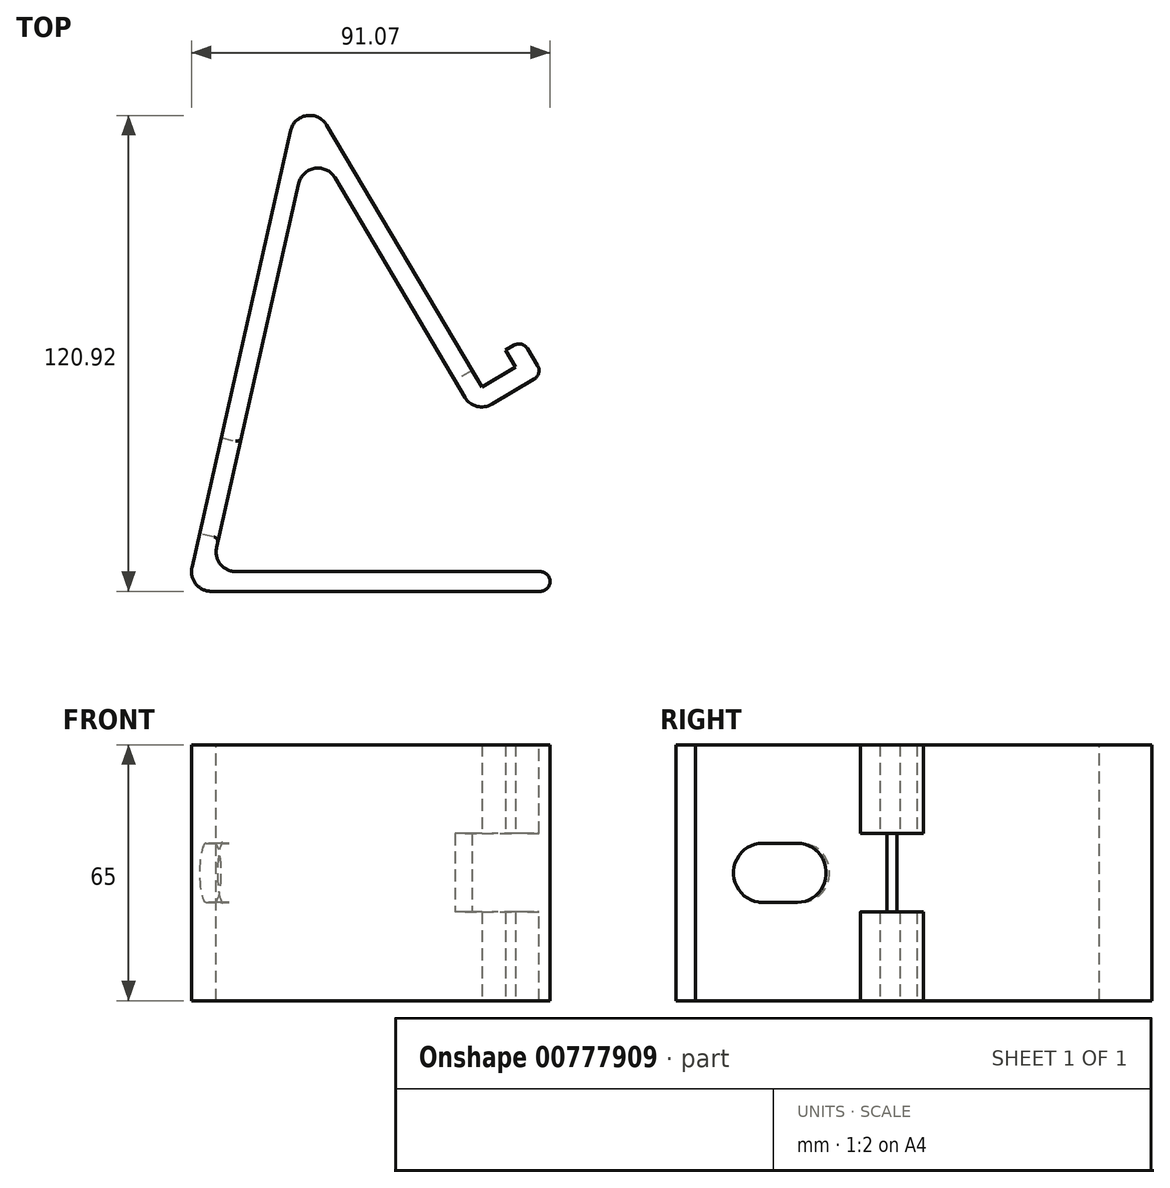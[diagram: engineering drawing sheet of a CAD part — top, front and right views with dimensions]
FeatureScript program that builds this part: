
annotation { "Feature Type Name" : "Feature", "Feature Type Description" : "" }
export const myFeature = defineFeature(function(context is Context, id is Id, definition is map)
    precondition{}
    {
        {
            var Q0;
            Q0=qCreatedBy(makeId("Top.planeOp"),FACE);
            var sketch = newSketch(context, id + "F0", { "sketchPlane" : qUnion([Q0])});
            skLineSegment(sketch, "E0", {"start": v(-95.14, -52.26) * mm, "end": v(-2.82, -52.26) * mm});
            skLineSegment(sketch, "E1", {"start": v(-2.82, -52.26) * mm, "end": v(-2.82, -47.26) * mm});
            skLineSegment(sketch, "E2", {"start": v(-2.82, -47.26) * mm, "end": v(-88.89, -47.26) * mm});
            skLineSegment(sketch, "E3", {"start": v(-88.89, -47.26) * mm, "end": v(-63.87, 63.66) * mm});
            skLineSegment(sketch, "E4", {"start": v(-63.87, 63.66) * mm, "end": v(-21.89, -7.26) * mm});
            skLineSegment(sketch, "E5", {"start": v(-21.89, -7.26) * mm, "end": v(-4.68, 2.93) * mm});
            skLineSegment(sketch, "E6", {"start": v(-20.13, -0.41) * mm, "end": v(-65.98, 77.04) * mm});
            skLineSegment(sketch, "E7", {"start": v(-20.13, -0.41) * mm, "end": v(-11.53, 4.68) * mm});
            skLineSegment(sketch, "E8", {"start": v(-11.53, 4.68) * mm, "end": v(-14.07, 8.99) * mm});
            skLineSegment(sketch, "E9", {"start": v(-14.07, 8.99) * mm, "end": v(-9.77, 11.53) * mm});
            skLineSegment(sketch, "E10", {"start": v(-9.77, 11.53) * mm, "end": v(-4.68, 2.93) * mm});
            skLineSegment(sketch, "E11", {"start": v(-65.98, 77.04) * mm, "end": v(-95.14, -52.26) * mm});
            skSolve(sketch);
        }
        {
            var Q0;
            Q0 = qSketchRegion(id + "F0", true);
            extrude(context, id + "F1", {"entities" : qUnion([Q0]), "depth" : 65 * mm, "offsetDistance" : 25 * mm});
        }
        {
            var Q0;
            Q0=makeQuery(id+"F1.opExtrude","SWEPT_FACE",FACE,{"disambiguationData":[OSD([sQuery(id+"F0.wireOp",EDGE,"E11")])]});
            var sketch = newSketch(context, id + "F2", { "sketchPlane" : qUnion([Q0])});
            skLineSegment(sketch, "E12.bottom", {"start": v(56.91, 40) * mm, "end": v(31.91, 40) * mm});
            skLineSegment(sketch, "E12.top", {"start": v(56.91, 25) * mm, "end": v(31.91, 25) * mm});
            skLineSegment(sketch, "E12.left", {"start": v(56.91, 40) * mm, "end": v(56.91, 25) * mm});
            skLineSegment(sketch, "E12.right", {"start": v(31.91, 40) * mm, "end": v(31.91, 25) * mm});
            skPoint(sketch, "E12.middle", {"position": v(44.41, 32.5) * mm});
            skSolve(sketch);
        }
        {
            var Q0;
            Q0=makeQuery(id+"F2.imprint","IMPRINT",FACE,{"disambiguationData":[TD([[makeQuery(id+"F2.imprint","IMPRINT",EDGE,{"derivedFrom":sQuery(id+"F2.wireOp",EDGE,"E12.bottom")}),1.0]])]});
            extrude(context, id + "F3", {"entities" : qUnion([Q0]), "operationType" : NewBodyOperationType.REMOVE, "oppositeDirection" : true, "depth" : 25 * mm, "offsetDistance" : 25 * mm});
        }
        {
            var Q0;
            Q0=makeQuery(id+"F1.opExtrude","SWEPT_FACE",FACE,{"disambiguationData":[OSD([sQuery(id+"F0.wireOp",EDGE,"E4")])]});
            var sketch = newSketch(context, id + "F4", { "sketchPlane" : qUnion([Q0])});
            skLineSegment(sketch, "E13.bottom", {"start": v(-4.9, 42.5) * mm, "end": v(-14.9, 42.5) * mm});
            skLineSegment(sketch, "E13.top", {"start": v(-4.9, 22.5) * mm, "end": v(-14.9, 22.5) * mm});
            skLineSegment(sketch, "E13.left", {"start": v(-4.9, 42.5) * mm, "end": v(-4.9, 22.5) * mm});
            skLineSegment(sketch, "E13.right", {"start": v(-14.9, 42.5) * mm, "end": v(-14.9, 22.5) * mm});
            skPoint(sketch, "E13.middle", {"position": v(-9.9, 32.5) * mm});
            skSolve(sketch);
        }
        {
            var Q0;
            Q0=makeQuery(id+"F4.imprint","IMPRINT",FACE,{"disambiguationData":[TD([[makeQuery(id+"F4.imprint","IMPRINT",EDGE,{"derivedFrom":sQuery(id+"F4.wireOp",EDGE,"E13.bottom")}),1.0]])]});
            extrude(context, id + "F5", {"entities" : qUnion([Q0]), "operationType" : NewBodyOperationType.REMOVE, "oppositeDirection" : true, "depth" : 25 * mm, "offsetDistance" : 25 * mm});
        }
        {
            var Q0;
            Q0=makeQuery(id+"F1.opExtrude","SWEPT_EDGE",EDGE,{"disambiguationData":[OSD([sQuery(id+"F0.wireOp",EDGE,"E0"),sQuery(id+"F0.wireOp",EDGE,"E11")])]});
            var Q1;
            Q1=makeQuery(id+"F1.opExtrude","SWEPT_EDGE",EDGE,{"disambiguationData":[OSD([sQuery(id+"F0.wireOp",EDGE,"E2"),sQuery(id+"F0.wireOp",EDGE,"E3")])]});
            var Q2;
            {var subQ0=sQuery(id+"F0.wireOp",EDGE,"E5");var subQ1=sQuery(id+"F0.wireOp",EDGE,"E4");Q2=makeQuery(id+"F5.boolean.opBoolean","SPLIT",EDGE,{"disambiguationData":[TD([makeQuery(id+"F5.opExtrude","SWEPT_FACE",FACE,{"disambiguationData":[OSD([sQuery(id+"F4.wireOp",EDGE,"E13.bottom")])]})])],"derivedFrom":makeQuery(id+"F1.opExtrude","SWEPT_EDGE",EDGE,{"disambiguationData":[OSD([subQ1,subQ0])]})});}
            var Q3;
            {var subQ0=sQuery(id+"F0.wireOp",EDGE,"E5");var subQ1=sQuery(id+"F0.wireOp",EDGE,"E4");Q3=makeQuery(id+"F5.boolean.opBoolean","SPLIT",EDGE,{"disambiguationData":[TD([makeQuery(id+"F5.opExtrude","SWEPT_FACE",FACE,{"disambiguationData":[OSD([sQuery(id+"F4.wireOp",EDGE,"E13.top")])]})])],"derivedFrom":makeQuery(id+"F1.opExtrude","SWEPT_EDGE",EDGE,{"disambiguationData":[OSD([subQ1,subQ0])]})});}
            var Q4;
            Q4=makeQuery(id+"F1.opExtrude","SWEPT_EDGE",EDGE,{"disambiguationData":[OSD([sQuery(id+"F0.wireOp",EDGE,"E3"),sQuery(id+"F0.wireOp",EDGE,"E4")])]});
            var Q5;
            Q5=makeQuery(id+"F1.opExtrude","SWEPT_EDGE",EDGE,{"disambiguationData":[OSD([sQuery(id+"F0.wireOp",EDGE,"E6"),sQuery(id+"F0.wireOp",EDGE,"E11")])]});
            fillet(context, id + "F6", {"entities" : qUnion([Q0, Q1, Q2, Q3, Q4, Q5]), "radius" : 5 * mm, "tangentPropagation" : true, "allowEdgeOverflow" : false});
        }
        {
            var Q0;
            {var subQ0=sQuery(id+"F0.wireOp",EDGE,"E10");var subQ1=sQuery(id+"F0.wireOp",EDGE,"E9");Q0=makeQuery(id+"F5.boolean.opBoolean","SPLIT",EDGE,{"disambiguationData":[TD([makeQuery(id+"F5.opExtrude","SWEPT_FACE",FACE,{"disambiguationData":[OSD([sQuery(id+"F4.wireOp",EDGE,"E13.top")])]})])],"derivedFrom":makeQuery(id+"F1.opExtrude","SWEPT_EDGE",EDGE,{"disambiguationData":[OSD([subQ1,subQ0])]})});}
            var Q1;
            {var subQ0=sQuery(id+"F0.wireOp",EDGE,"E10");var subQ1=sQuery(id+"F0.wireOp",EDGE,"E9");Q1=makeQuery(id+"F5.boolean.opBoolean","SPLIT",EDGE,{"disambiguationData":[TD([makeQuery(id+"F5.opExtrude","SWEPT_FACE",FACE,{"disambiguationData":[OSD([sQuery(id+"F4.wireOp",EDGE,"E13.bottom")])]})])],"derivedFrom":makeQuery(id+"F1.opExtrude","SWEPT_EDGE",EDGE,{"disambiguationData":[OSD([subQ1,subQ0])]})});}
            var Q2;
            {var subQ0=sQuery(id+"F0.wireOp",EDGE,"E10");var subQ1=sQuery(id+"F0.wireOp",EDGE,"E5");Q2=makeQuery(id+"F5.boolean.opBoolean","SPLIT",EDGE,{"disambiguationData":[TD([makeQuery(id+"F5.opExtrude","SWEPT_FACE",FACE,{"disambiguationData":[OSD([sQuery(id+"F4.wireOp",EDGE,"E13.bottom")])]})])],"derivedFrom":makeQuery(id+"F1.opExtrude","SWEPT_EDGE",EDGE,{"disambiguationData":[OSD([subQ1,subQ0])]})});}
            var Q3;
            {var subQ0=sQuery(id+"F0.wireOp",EDGE,"E10");var subQ1=sQuery(id+"F0.wireOp",EDGE,"E5");Q3=makeQuery(id+"F5.boolean.opBoolean","SPLIT",EDGE,{"disambiguationData":[TD([makeQuery(id+"F5.opExtrude","SWEPT_FACE",FACE,{"disambiguationData":[OSD([sQuery(id+"F4.wireOp",EDGE,"E13.top")])]})])],"derivedFrom":makeQuery(id+"F1.opExtrude","SWEPT_EDGE",EDGE,{"disambiguationData":[OSD([subQ1,subQ0])]})});}
            fillet(context, id + "F7", {"entities" : qUnion([Q0, Q1, Q2, Q3]), "radius" : 2.5 * mm, "tangentPropagation" : true, "allowEdgeOverflow" : false});
        }
        {
            var Q0;
            Q0=makeQuery(id+"F3.boolean.opBoolean","COPY",EDGE,{"derivedFrom":makeQuery(id+"F3.opExtrude","SWEPT_EDGE",EDGE,{"disambiguationData":[OSD([sQuery(id+"F2.wireOp",EDGE,"E12.bottom"),sQuery(id+"F2.wireOp",EDGE,"E12.right")])]})});
            var Q1;
            Q1=makeQuery(id+"F3.boolean.opBoolean","COPY",EDGE,{"derivedFrom":makeQuery(id+"F3.opExtrude","SWEPT_EDGE",EDGE,{"disambiguationData":[OSD([sQuery(id+"F2.wireOp",EDGE,"E12.top"),sQuery(id+"F2.wireOp",EDGE,"E12.right")])]})});
            var Q2;
            Q2=makeQuery(id+"F3.boolean.opBoolean","COPY",EDGE,{"derivedFrom":makeQuery(id+"F3.opExtrude","SWEPT_EDGE",EDGE,{"disambiguationData":[OSD([sQuery(id+"F2.wireOp",EDGE,"E12.bottom"),sQuery(id+"F2.wireOp",EDGE,"E12.left")])]})});
            var Q3;
            Q3=makeQuery(id+"F3.boolean.opBoolean","COPY",EDGE,{"derivedFrom":makeQuery(id+"F3.opExtrude","SWEPT_EDGE",EDGE,{"disambiguationData":[OSD([sQuery(id+"F2.wireOp",EDGE,"E12.top"),sQuery(id+"F2.wireOp",EDGE,"E12.left")])]})});
            fillet(context, id + "F8", {"entities" : qUnion([Q0, Q1, Q2, Q3]), "radius" : 7.5 * mm, "tangentPropagation" : true, "allowEdgeOverflow" : false});
        }
        {
            var Q0;
            Q0=makeQuery(id+"F1.opExtrude","SWEPT_EDGE",EDGE,{"disambiguationData":[OSD([sQuery(id+"F0.wireOp",EDGE,"E0"),sQuery(id+"F0.wireOp",EDGE,"E1")])]});
            var Q1;
            Q1=makeQuery(id+"F1.opExtrude","SWEPT_EDGE",EDGE,{"disambiguationData":[OSD([sQuery(id+"F0.wireOp",EDGE,"E1"),sQuery(id+"F0.wireOp",EDGE,"E2")])]});
            fillet(context, id + "F9", {"entities" : qUnion([Q0, Q1]), "radius" : 2.5 * mm, "tangentPropagation" : true, "allowEdgeOverflow" : false});
        }
        {
            var Q0;
            Q0=makeQuery(id+"F8.opFillet","BLEND_EDGE",EDGE,{"blendedFrom":[makeQuery(id+"F3.boolean.opBoolean","COPY",EDGE,{"derivedFrom":makeQuery(id+"F3.opExtrude","SWEPT_EDGE",EDGE,{"disambiguationData":[OSD([sQuery(id+"F2.wireOp",EDGE,"E12.top"),sQuery(id+"F2.wireOp",EDGE,"E12.right")])]})}),makeQuery(id+"F1.opExtrude","SWEPT_FACE",FACE,{"disambiguationData":[OSD([sQuery(id+"F0.wireOp",EDGE,"E11")])]})],"blendedInto":[makeQuery(id+"F1.opExtrude","SWEPT_FACE",FACE,{"disambiguationData":[OSD([sQuery(id+"F0.wireOp",EDGE,"E11")])]})]});
            var Q1;
            Q1=makeQuery(id+"F3.boolean.opBoolean","INTERSECT",EDGE,{"derivedFrom":[makeQuery(id+"F1.opExtrude","SWEPT_FACE",FACE,{"disambiguationData":[OSD([sQuery(id+"F0.wireOp",EDGE,"E3")])]}),makeQuery(id+"F3.opExtrude","SWEPT_FACE",FACE,{"disambiguationData":[OSD([sQuery(id+"F2.wireOp",EDGE,"E12.bottom")])]})]});
            fillet(context, id + "F10", {"entities" : qUnion([Q0, Q1]), "radius" : 1.25 * mm, "tangentPropagation" : true, "allowEdgeOverflow" : false});
        }
    });
